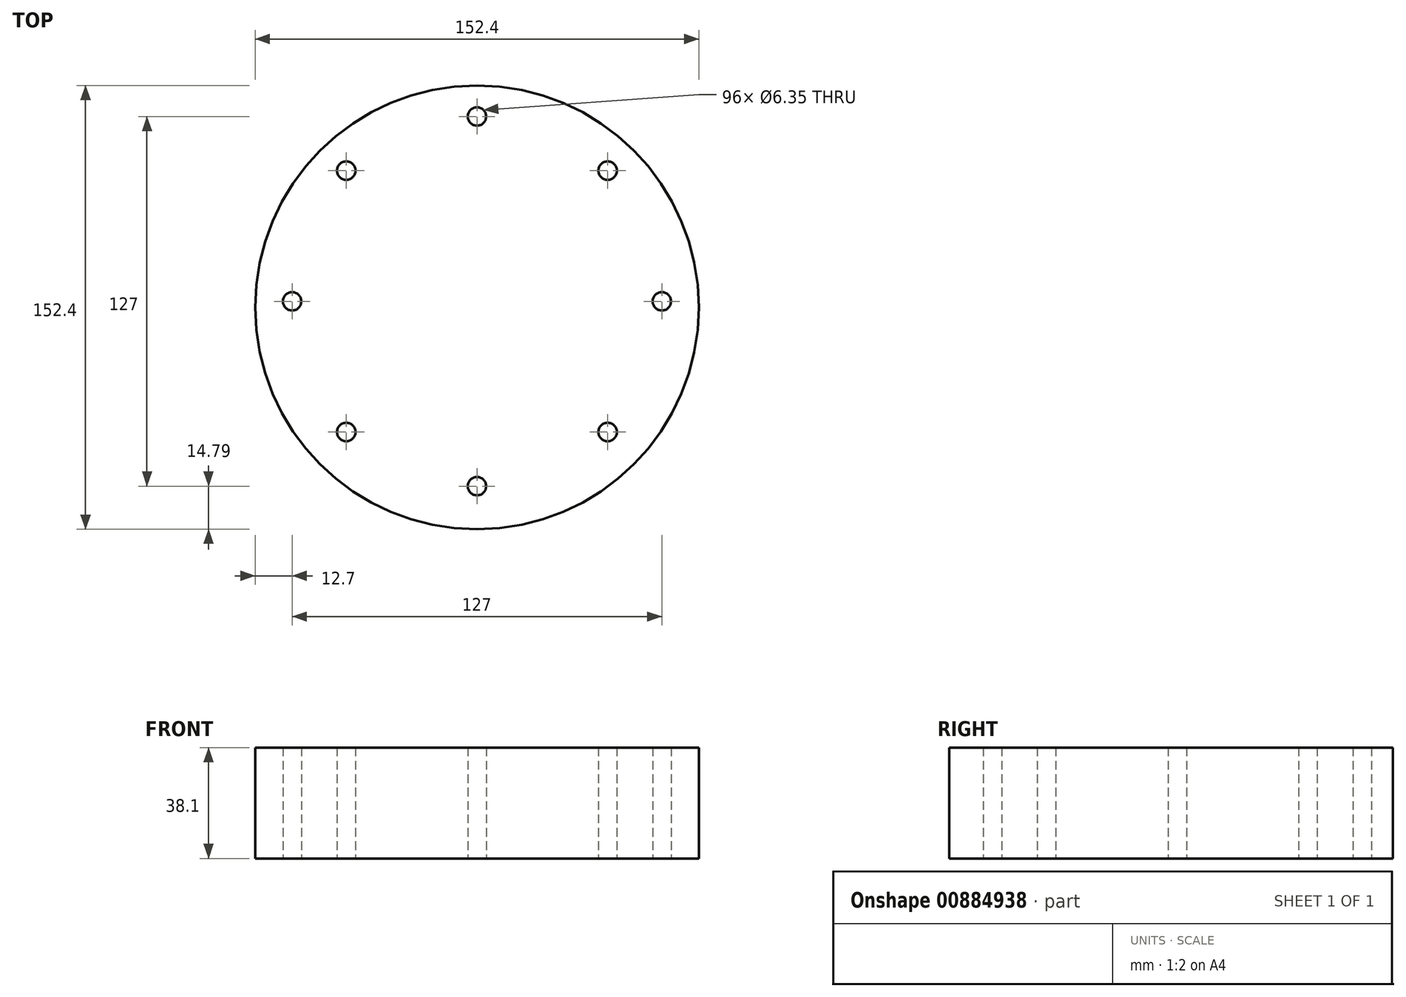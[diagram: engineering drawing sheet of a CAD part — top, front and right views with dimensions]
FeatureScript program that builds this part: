
annotation { "Feature Type Name" : "Feature", "Feature Type Description" : "" }
export const myFeature = defineFeature(function(context is Context, id is Id, definition is map)
    precondition{}
    {
        {
            var Q0;
            Q0=qCreatedBy(makeId("Top.planeOp"),FACE);
            var sketch = newSketch(context, id + "F0", { "sketchPlane" : qUnion([Q0])});
            skCircle(sketch, "E0", {"center": v(0, 0) * mm, "radius": 76.2 * mm});
            skCircle(sketch, "E1", {"center": v(0, 65.59) * mm, "radius": 3.18 * mm});
            skCircle(sketch, "E2.1.0", {"center": v(-44.9, 47) * mm, "radius": 3.18 * mm});
            skCircle(sketch, "E2.2.0", {"center": v(-63.5, 2.09) * mm, "radius": 3.18 * mm});
            skCircle(sketch, "E2.3.0", {"center": v(-44.9, -42.81) * mm, "radius": 3.18 * mm});
            skCircle(sketch, "E2.4.0", {"center": v(0, -61.41) * mm, "radius": 3.18 * mm});
            skCircle(sketch, "E2.5.0", {"center": v(44.9, -42.81) * mm, "radius": 3.18 * mm});
            skCircle(sketch, "E2.6.0", {"center": v(63.5, 2.09) * mm, "radius": 3.18 * mm});
            skCircle(sketch, "E2.7.0", {"center": v(44.9, 47) * mm, "radius": 3.18 * mm});
            skPoint(sketch, "E2.center", {"position": v(0, 2.09) * mm});
            skSolve(sketch);
        }
        {
            var Q0;
            Q0 = qSketchRegion(id + "F0", true);
            extrude(context, id + "F1", {"entities" : qUnion([Q0]), "depth" : 38.1 * mm, "offsetDistance" : 25.4 * mm});
        }
    });
